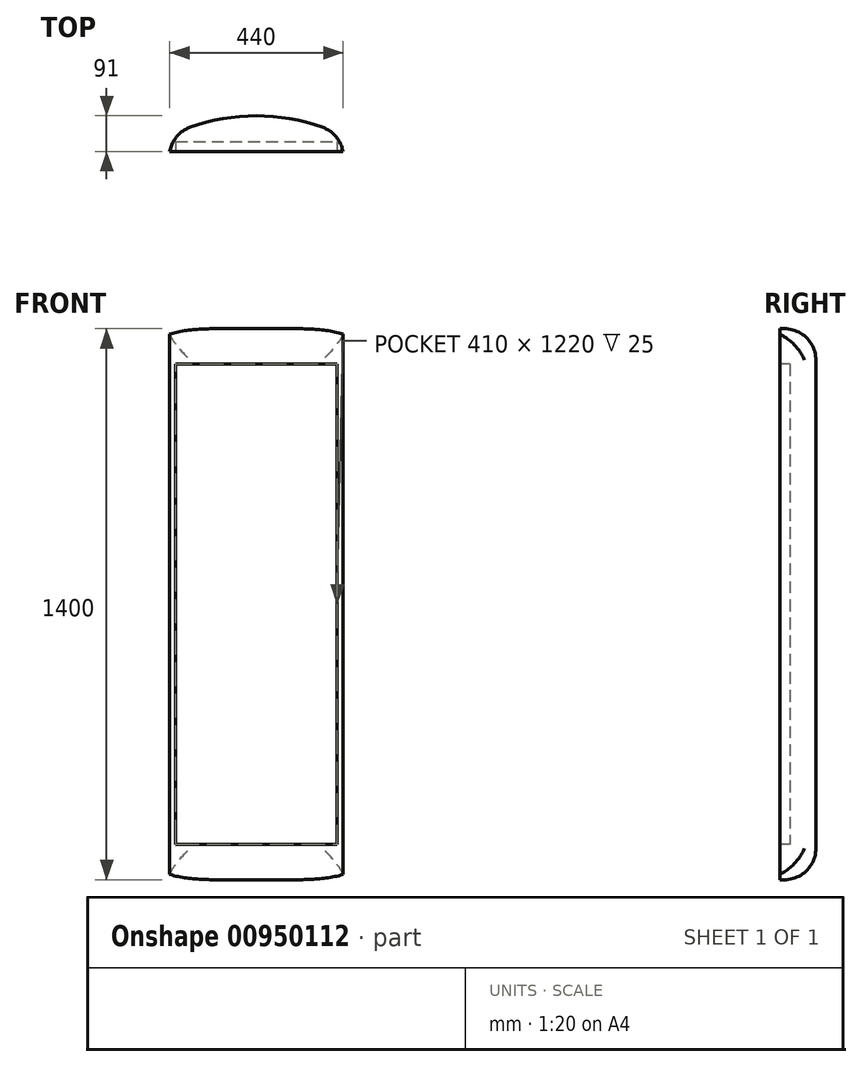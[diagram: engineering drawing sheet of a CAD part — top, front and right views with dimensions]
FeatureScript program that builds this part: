
annotation { "Feature Type Name" : "Feature", "Feature Type Description" : "" }
export const myFeature = defineFeature(function(context is Context, id is Id, definition is map)
    precondition{}
    {
        {
            var Q0;
            Q0=qCreatedBy(makeId("Top.planeOp"),FACE);
            var sketch = newSketch(context, id + "F0", { "sketchPlane" : qUnion([Q0])});
            skLineSegment(sketch, "E0.bottom", {"start": v(220, -20) * mm, "end": v(-220, -20) * mm});
            skLineSegment(sketch, "E0.top", {"start": v(220, 20) * mm, "end": v(-220, 20) * mm});
            skLineSegment(sketch, "E0.left", {"start": v(220, -20) * mm, "end": v(220, 20) * mm});
            skLineSegment(sketch, "E0.right", {"start": v(-220, -20) * mm, "end": v(-220, 20) * mm});
            skPoint(sketch, "E0.middle", {"position": v(0, 0) * mm});
            skArc(sketch, "E1", {"start": v(-220, 20) * mm, "mid": v(0, 71) * mm, "end": v(220, 20) * mm});
            skSolve(sketch);
        }
        {
            var Q0;
            Q0=makeQuery(id+"F0.imprint","IMPRINT",FACE,{"disambiguationData":[TD([[makeQuery(id+"F0.imprint","IMPRINT",EDGE,{"derivedFrom":sQuery(id+"F0.wireOp",EDGE,"E0.bottom")}),-1.0]])]});
            var Q1;
            Q1=makeQuery(id+"F0.imprint","IMPRINT",FACE,{"disambiguationData":[TD([[makeQuery(id+"F0.imprint","IMPRINT",EDGE,{"derivedFrom":sQuery(id+"F0.wireOp",EDGE,"E0.top")}),-1.0]])]});
            extrude(context, id + "F1", {"entities" : qUnion([Q0, Q1]), "endBound" : BoundingType.SYMMETRIC, "depth" : 1400 * mm, "offsetDistance" : 25 * mm});
        }
        {
            var Q0;
            Q0=makeQuery(id+"F1.opExtrude","SWEPT_FACE",FACE,{"disambiguationData":[OSD([sQuery(id+"F0.wireOp",EDGE,"E0.bottom")])]});
            var sketch = newSketch(context, id + "F2", { "sketchPlane" : qUnion([Q0])});
            skLineSegment(sketch, "E2.bottom", {"start": v(-205, 610) * mm, "end": v(205, 610) * mm});
            skLineSegment(sketch, "E2.top", {"start": v(-205, -610) * mm, "end": v(205, -610) * mm});
            skLineSegment(sketch, "E2.left", {"start": v(-205, 610) * mm, "end": v(-205, -610) * mm});
            skLineSegment(sketch, "E2.right", {"start": v(205, 610) * mm, "end": v(205, -610) * mm});
            skPoint(sketch, "E2.middle", {"position": v(0, 0) * mm});
            skSolve(sketch);
        }
        {
            var Q0;
            Q0=makeQuery(id+"F2.imprint","IMPRINT",FACE,{"disambiguationData":[TD([[makeQuery(id+"F2.imprint","IMPRINT",EDGE,{"derivedFrom":sQuery(id+"F2.wireOp",EDGE,"E2.bottom")}),-1.0]])]});
            extrude(context, id + "F3", {"entities" : qUnion([Q0]), "operationType" : NewBodyOperationType.REMOVE, "oppositeDirection" : true, "depth" : 25 * mm, "offsetDistance" : 25 * mm});
        }
        {
            var Q0;
            Q0=makeQuery(id+"F1.opExtrude","CAP_EDGE",EDGE,{"disambiguationData":[OSD([sQuery(id+"F0.wireOp",EDGE,"E1")])],"isStart":false});
            var Q1;
            Q1=makeQuery(id+"F1.opExtrude","CAP_EDGE",EDGE,{"disambiguationData":[OSD([sQuery(id+"F0.wireOp",EDGE,"E1")])],"isStart":true});
            var Q2;
            Q2=makeQuery(id+"F1.opExtrude","SWEPT_EDGE",EDGE,{"disambiguationData":[OSD([sQuery(id+"F0.wireOp",EDGE,"E0.top"),sQuery(id+"F0.wireOp",EDGE,"E0.left"),sQuery(id+"F0.wireOp",EDGE,"E1")])]});
            var Q3;
            Q3=makeQuery(id+"F1.opExtrude","SWEPT_EDGE",EDGE,{"disambiguationData":[OSD([sQuery(id+"F0.wireOp",EDGE,"E0.top"),sQuery(id+"F0.wireOp",EDGE,"E0.right"),sQuery(id+"F0.wireOp",EDGE,"E1")])]});
            fillet(context, id + "F4", {"entities" : qUnion([Q0, Q1, Q2, Q3]), "radius" : 80 * mm, "tangentPropagation" : true, "allowEdgeOverflow" : false});
        }
    });
